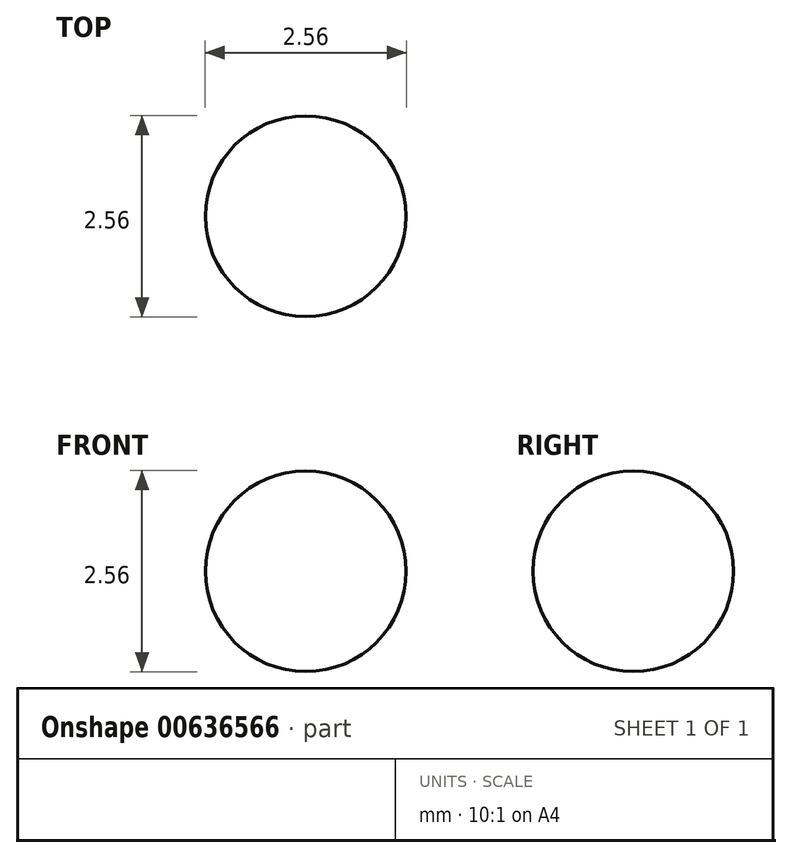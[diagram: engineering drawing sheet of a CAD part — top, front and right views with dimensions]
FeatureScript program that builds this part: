
annotation { "Feature Type Name" : "Feature", "Feature Type Description" : "" }
export const myFeature = defineFeature(function(context is Context, id is Id, definition is map)
    precondition{}
    {
        {
            var Q0;
            Q0=qCreatedBy(makeId("Top.planeOp"),FACE);
            var sketch = newSketch(context, id + "F0", { "sketchPlane" : qUnion([Q0])});
            skArc(sketch, "E0", {"start": v(0, -1.28) * mm, "mid": v(1.28, 0) * mm, "end": v(0, 1.28) * mm});
            skLineSegment(sketch, "E1", {"start": v(0, 1.27) * mm, "end": v(0, -1.27) * mm});
            skSolve(sketch);
        }
        {
            var Q0;
            Q0 = qSketchRegion(id + "F0", true);
            var Q1;
            Q1=sQuery(id+"F0.wireOp",EDGE,"E1");
            revolve(context, id + "F1", {"entities" : qUnion([Q0]), "axis" : qUnion([Q1]), "revolveType" : RevolveType.FULL});
        }
    });
